# Revit family: НЕВАТОМ_Зонт крышный_20220407
name_source: partatom
category: Воздухораспределители
revit_build: Autodesk Revit 2017 (Build: 20170118_1100(x64)
units: mm (PartAtom-declared; Revit-internal decimal feet)

## family parameters
Всегда вертикально = Нет
На основе рабочей плоскости = Нет
Общий = Нет
При загрузке вырезать с полостями = Нет
Размер круглого соединителя = Использовать диаметр
Тип детали = Нормальный
Точка расчета площади = Нет

## types (18) — shared parameters
ADSK_Единица измерения = шт
ADSK_Завод-изготовитель = NEVATOM
ADSK_Масса_Текст = кг
ADSK_Материал наименование = Оцинкованная сталь
ADSK_Наименование = ЗОНТ КРЫШНЫЙ
ADSK_Потеря давления воздуха = 0.0 Па
ADSK_Расход воздуха = 0.0 л/с
Nevatom_URL = https://t.me
zero-valued in all types: ADSK_Масса

## per-type parameters (varying)
| type | A | ADSK_Размер_Высота | ADSK_Размер_Длина | ADSK_Размер_Ширина | D | D* | D*/2 | Dk | H | Hк | k | матерал корпуса |
| 100 | 35 мм | 130 мм | 170 мм | 170 мм | 100 мм | 5 мм | 3 мм | 170 мм | 130 мм | 43 мм | 135 мм | Материал корпуса |
| 125 | 35 мм | 155 мм | 215 мм | 215 мм | 125 мм | 6 мм | 3 мм | 215 мм | 155 мм | 52 мм | 170 мм | <По категории> |
| 160 | 35 мм | 180 мм | 275 мм | 275 мм | 160 мм | 8 мм | 4 мм | 275 мм | 180 мм | 60 мм | 218 мм | <По категории> |
| 180 | 35 мм | 185 мм | 300 мм | 300 мм | 180 мм | 9 мм | 5 мм | 300 мм | 185 мм | 62 мм | 240 мм | <По категории> |
| 200 | 35 мм | 215 мм | 340 мм | 340 мм | 200 мм | 10 мм | 5 мм | 340 мм | 215 мм | 72 мм | 270 мм | <По категории> |
| 225 | 35 мм | 235 мм | 382 мм | 382 мм | 225 мм | 11 мм | 6 мм | 382 мм | 235 мм | 78 мм | 304 мм | <По категории> |
| 250 | 35 мм | 252 мм | 430 мм | 430 мм | 250 мм | 13 мм | 6 мм | 430 мм | 252 мм | 84 мм | 340 мм | Материал корпуса |
| 315 | 35 мм | 295 мм | 540 мм | 540 мм | 315 мм | 16 мм | 8 мм | 540 мм | 295 мм | 98 мм | 428 мм | <По категории> |
| 355 | 55 мм | 347 мм | 630 мм | 630 мм | 355 мм | 18 мм | 9 мм | 630 мм | 347 мм | 116 мм | 493 мм | <По категории> |
| 400 | 55 мм | 375 мм | 700 мм | 700 мм | 400 мм | 20 мм | 10 мм | 700 мм | 375 мм | 125 мм | 550 мм | <По категории> |
| 450 | 55 мм | 410 мм | 770 мм | 770 мм | 450 мм | 23 мм | 11 мм | 770 мм | 410 мм | 137 мм | 610 мм | <По категории> |
| 500 | 55 мм | 495 мм | 900 мм | 900 мм | 500 мм | 25 мм | 13 мм | 900 мм | 495 мм | 165 мм | 700 мм | <По категории> |
| 560 | 55 мм | 517 мм | 950 мм | 950 мм | 560 мм | 28 мм | 14 мм | 950 мм | 517 мм | 172 мм | 755 мм | <По категории> |
| 630 | 55 мм | 538 мм | 1130 мм | 1130 мм | 630 мм | 32 мм | 16 мм | 1130 мм | 538 мм | 179 мм | 880 мм | <По категории> |
| 710 | 55 мм | 600 мм | 1300 мм | 1300 мм | 710 мм | 36 мм | 18 мм | 1300 мм | 600 мм | 200 мм | 1005 мм | <По категории> |
| 800 | 55 мм | 667 мм | 1450 мм | 1450 мм | 800 мм | 40 мм | 20 мм | 1450 мм | 667 мм | 222 мм | 1125 мм | <По категории> |
| 1000 | 100 мм | 942 мм | 1800 мм | 1800 мм | 1000 мм | 50 мм | 25 мм | 1800 мм | 942 мм | 314 мм | 1400 мм | <По категории> |
| 1250 | 100 мм | 1100 мм | 2100 мм | 2100 мм | 1250 мм | 63 мм | 31 мм | 2100 мм | 1100 мм | 367 мм | 1675 мм | Материал корпуса |

note: column(s) folded — value = type name in every type: ADSK_Марка
